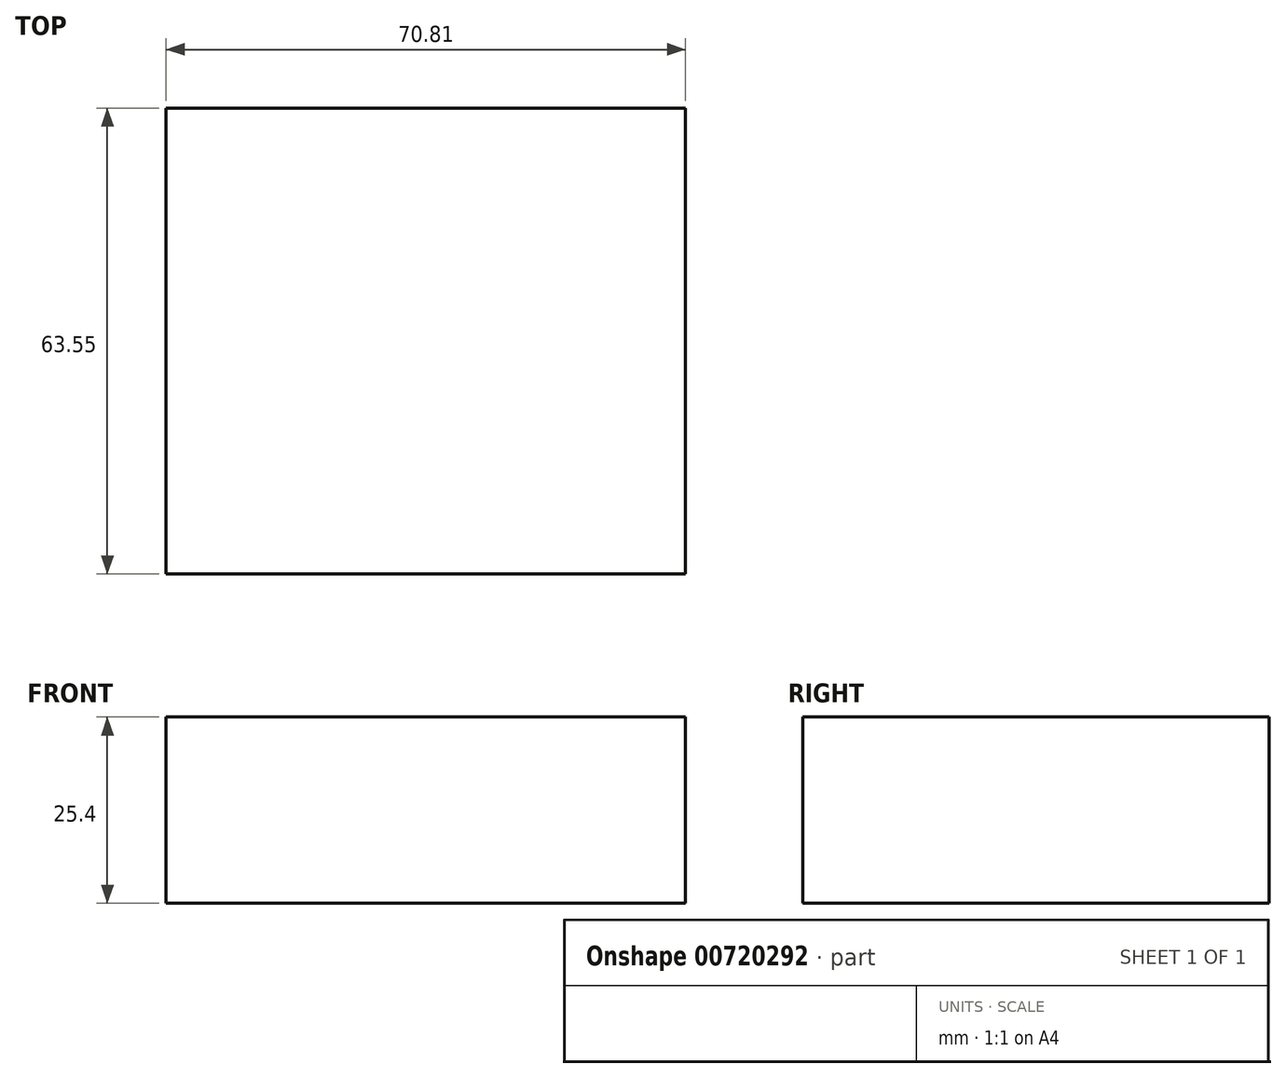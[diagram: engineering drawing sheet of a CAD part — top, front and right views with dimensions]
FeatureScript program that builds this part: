
annotation { "Feature Type Name" : "Feature", "Feature Type Description" : "" }
export const myFeature = defineFeature(function(context is Context, id is Id, definition is map)
    precondition{}
    {
        {
            var Q0;
            Q0=qCreatedBy(makeId("Top.planeOp"),FACE);
            var sketch = newSketch(context, id + "F0", { "sketchPlane" : qUnion([Q0])});
            skLineSegment(sketch, "E0.bottom", {"start": v(-27.66, -41.55) * mm, "end": v(43.15, -41.55) * mm});
            skLineSegment(sketch, "E0.top", {"start": v(-27.66, 22) * mm, "end": v(43.15, 22) * mm});
            skLineSegment(sketch, "E0.left", {"start": v(-27.66, -41.55) * mm, "end": v(-27.66, 22) * mm});
            skLineSegment(sketch, "E0.right", {"start": v(43.15, -41.55) * mm, "end": v(43.15, 22) * mm});
            skSolve(sketch);
        }
        {
            var Q0;
            Q0=makeQuery(id+"F0.imprint","IMPRINT",FACE,{"disambiguationData":[TD([[makeQuery(id+"F0.imprint","IMPRINT",EDGE,{"derivedFrom":sQuery(id+"F0.wireOp",EDGE,"E0.bottom")}),1.0]])]});
            extrude(context, id + "F1", {"entities" : qUnion([Q0]), "depth" : 25.4 * mm, "offsetDistance" : 25.4 * mm});
        }
    });
